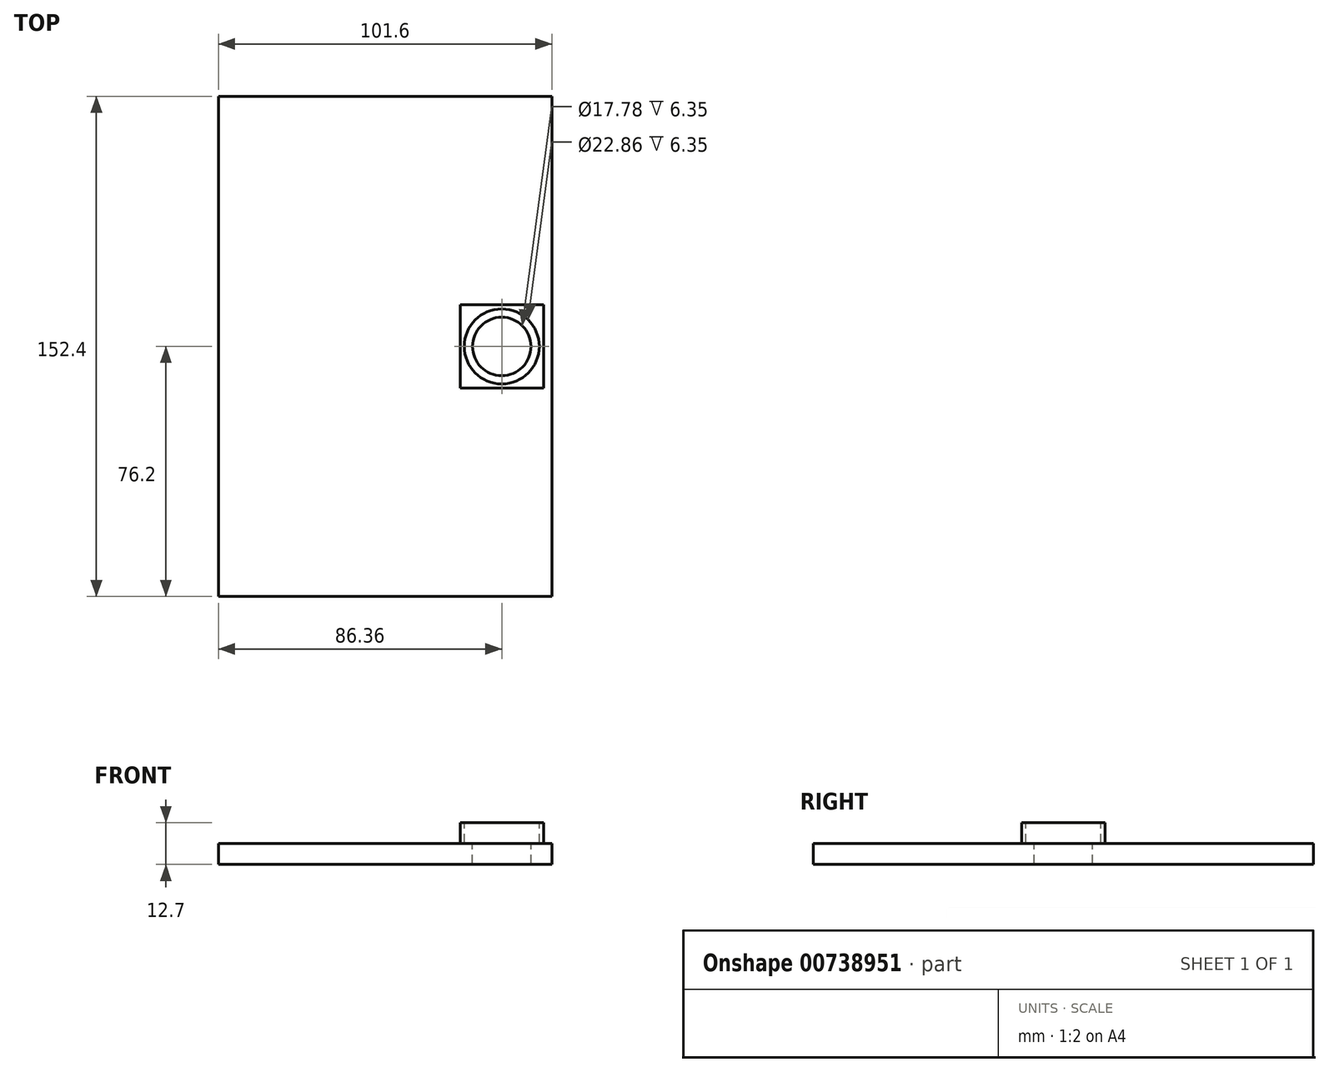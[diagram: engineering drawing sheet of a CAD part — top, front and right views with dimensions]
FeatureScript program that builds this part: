
annotation { "Feature Type Name" : "Feature", "Feature Type Description" : "" }
export const myFeature = defineFeature(function(context is Context, id is Id, definition is map)
    precondition{}
    {
        {
            var Q0;
            Q0=qCreatedBy(makeId("Top.planeOp"),FACE);
            var sketch = newSketch(context, id + "F0", { "sketchPlane" : qUnion([Q0])});
            skLineSegment(sketch, "E0.bottom", {"start": v(-50.8, 76.2) * mm, "end": v(50.8, 76.2) * mm});
            skLineSegment(sketch, "E0.top", {"start": v(-50.8, -76.2) * mm, "end": v(50.8, -76.2) * mm});
            skLineSegment(sketch, "E0.left", {"start": v(-50.8, 76.2) * mm, "end": v(-50.8, -76.2) * mm});
            skLineSegment(sketch, "E0.right", {"start": v(50.8, 76.2) * mm, "end": v(50.8, -76.2) * mm});
            skPoint(sketch, "E0.middle", {"position": v(0, 0) * mm});
            skPoint(sketch, "E1", {"position": v(35.56, 0) * mm});
            skLineSegment(sketch, "E2", {"start": v(35.56, 0) * mm, "end": v(50.8, 0) * mm});
            skLineSegment(sketch, "E3.bottom", {"start": v(48.26, -12.7) * mm, "end": v(22.86, -12.7) * mm});
            skLineSegment(sketch, "E3.top", {"start": v(48.26, 12.7) * mm, "end": v(22.86, 12.7) * mm});
            skLineSegment(sketch, "E3.left", {"start": v(48.26, -12.7) * mm, "end": v(48.26, 12.7) * mm});
            skLineSegment(sketch, "E3.right", {"start": v(22.86, -12.7) * mm, "end": v(22.86, 12.7) * mm});
            skSolve(sketch);
        }
        {
            var Q0;
            {var subQ1=sQuery(id+"F0.wireOp",EDGE,"E0.bottom");Q0=makeQuery(id+"F0.imprint","IMPRINT",FACE,{"disambiguationData":[TD([[makeQuery(id+"F0.imprint","IMPRINT",EDGE,{"derivedFrom":subQ1}),-1.0]])]});}
            extrude(context, id + "F1", {"entities" : qUnion([Q0]), "depth" : 6.35 * mm, "offsetDistance" : 25.4 * mm});
        }
        {
            var Q0;
            {var subQ3=sQuery(id+"F0.wireOp",EDGE,"E3.bottom");Q0=makeQuery(id+"F0.imprint","IMPRINT",FACE,{"disambiguationData":[TD([[makeQuery(id+"F0.imprint","IMPRINT",EDGE,{"derivedFrom":subQ3}),-1.0]])]});}
            extrude(context, id + "F2", {"entities" : qUnion([Q0]), "operationType" : NewBodyOperationType.ADD, "depth" : 12.7 * mm, "offsetDistance" : 25.4 * mm});
        }
        {
            var Q0;
            Q0=makeQuery(id+"F2.opExtrude","CAP_FACE",FACE,{"disambiguationData":[OSD([sQuery(id+"F0.wireOp",EDGE,"E3.bottom"),sQuery(id+"F0.wireOp",EDGE,"E3.top"),sQuery(id+"F0.wireOp",EDGE,"E3.left"),sQuery(id+"F0.wireOp",EDGE,"E3.right")])],"isStart":false});
            var sketch = newSketch(context, id + "F3", { "sketchPlane" : qUnion([Q0])});
            skPoint(sketch, "E4", {"position": v(35.56, 0) * mm});
            skLineSegment(sketch, "E5", {"start": v(35.56, 0) * mm, "end": v(48.26, 0) * mm});
            skLineSegment(sketch, "E6", {"start": v(35.56, 0) * mm, "end": v(35.56, -12.7) * mm});
            skSolve(sketch);
        }
        {
            var Q0;
            Q0=sQuery(id+"F3.wireOp",VERTEX,"E4");
            var Q1;
            Q1=makeQuery(id+"F1.opExtrude","SWEPT_BODY",BODY,{"disambiguationData":[OSD([sQuery(id+"F0.wireOp",EDGE,"E0.bottom"),sQuery(id+"F0.wireOp",EDGE,"E0.top"),sQuery(id+"F0.wireOp",EDGE,"E0.left"),sQuery(id+"F0.wireOp",EDGE,"E0.right"),sQuery(id+"F0.wireOp",EDGE,"E3.bottom"),sQuery(id+"F0.wireOp",EDGE,"E3.top"),sQuery(id+"F0.wireOp",EDGE,"E3.left"),sQuery(id+"F0.wireOp",EDGE,"E3.right")])]});
            hole(context, id + "F4", {"style" : HoleStyle.C_BORE, "endStyle" : HoleEndStyle.THROUGH, "holeDiameter" : 17.78 * mm, "cBoreDiameter" : 22.86 * mm, "cBoreDepth" : 6.35 * mm, "majorDiameter" : 6.35 * mm, "isTappedThrough" : true, "tappedDepth" : 12.7 * mm, "tapClearance" : 3, "locations" : qUnion([Q0]), "scope" : qUnion([Q1])});
        }
    });
